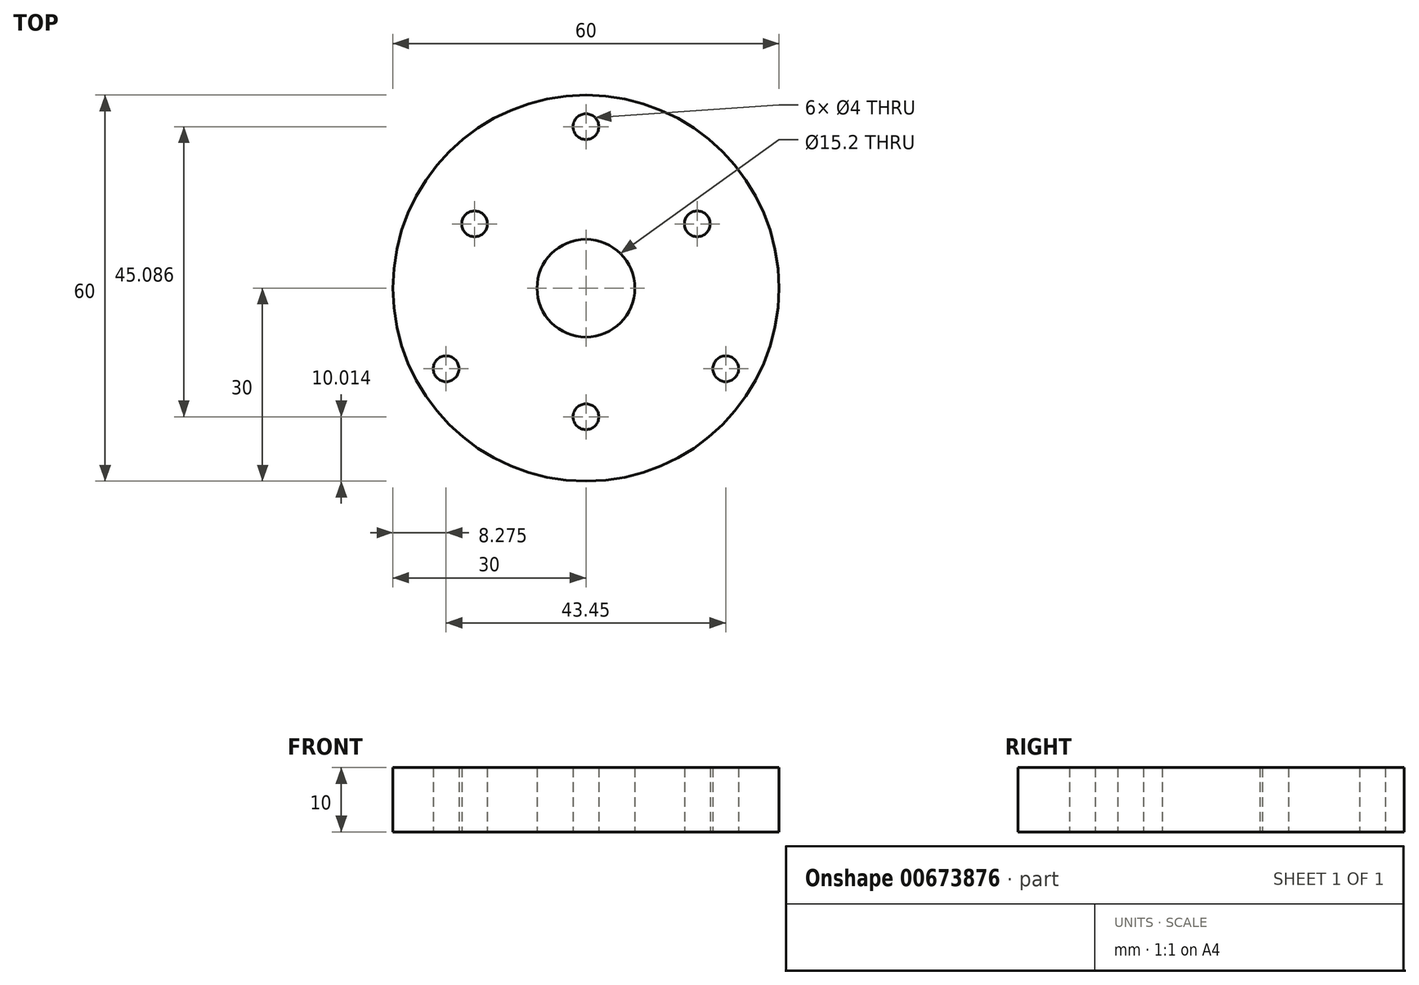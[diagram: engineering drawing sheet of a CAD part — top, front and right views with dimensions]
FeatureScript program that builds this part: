
annotation { "Feature Type Name" : "Feature", "Feature Type Description" : "" }
export const myFeature = defineFeature(function(context is Context, id is Id, definition is map)
    precondition{}
    {
        {
            var Q0;
            Q0=qCreatedBy(makeId("Top.planeOp"),FACE);
            var sketch = newSketch(context, id + "F0", { "sketchPlane" : qUnion([Q0])});
            skCircle(sketch, "E0", {"center": v(0, 0) * mm, "radius": 30 * mm});
            skCircle(sketch, "E1", {"center": v(0, 0) * mm, "radius": 7.6 * mm});
            skCircle(sketch, "E2", {"center": v(0, 25.1) * mm, "radius": 2 * mm});
            skCircle(sketch, "E3.1.0", {"center": v(21.73, -12.53) * mm, "radius": 2 * mm});
            skCircle(sketch, "E3.2.0", {"center": v(-21.73, -12.53) * mm, "radius": 2 * mm});
            skPoint(sketch, "E3.center", {"position": v(0, 0.01) * mm});
            skCircle(sketch, "E4", {"center": v(0, -19.99) * mm, "radius": 2 * mm});
            skCircle(sketch, "E5.1.0", {"center": v(17.3, 10) * mm, "radius": 2 * mm});
            skCircle(sketch, "E5.2.0", {"center": v(-17.3, 10) * mm, "radius": 2 * mm});
            skSolve(sketch);
        }
        {
            var Q0;
            Q0=makeQuery(id+"F0.imprint","IMPRINT",FACE,{"disambiguationData":[TD([[makeQuery(id+"F0.imprint","IMPRINT",EDGE,{"derivedFrom":sQuery(id+"F0.wireOp",EDGE,"E0")}),1.0]])]});
            extrude(context, id + "F1", {"entities" : qUnion([Q0]), "depth" : 10 * mm, "offsetDistance" : 25 * mm});
        }
    });
